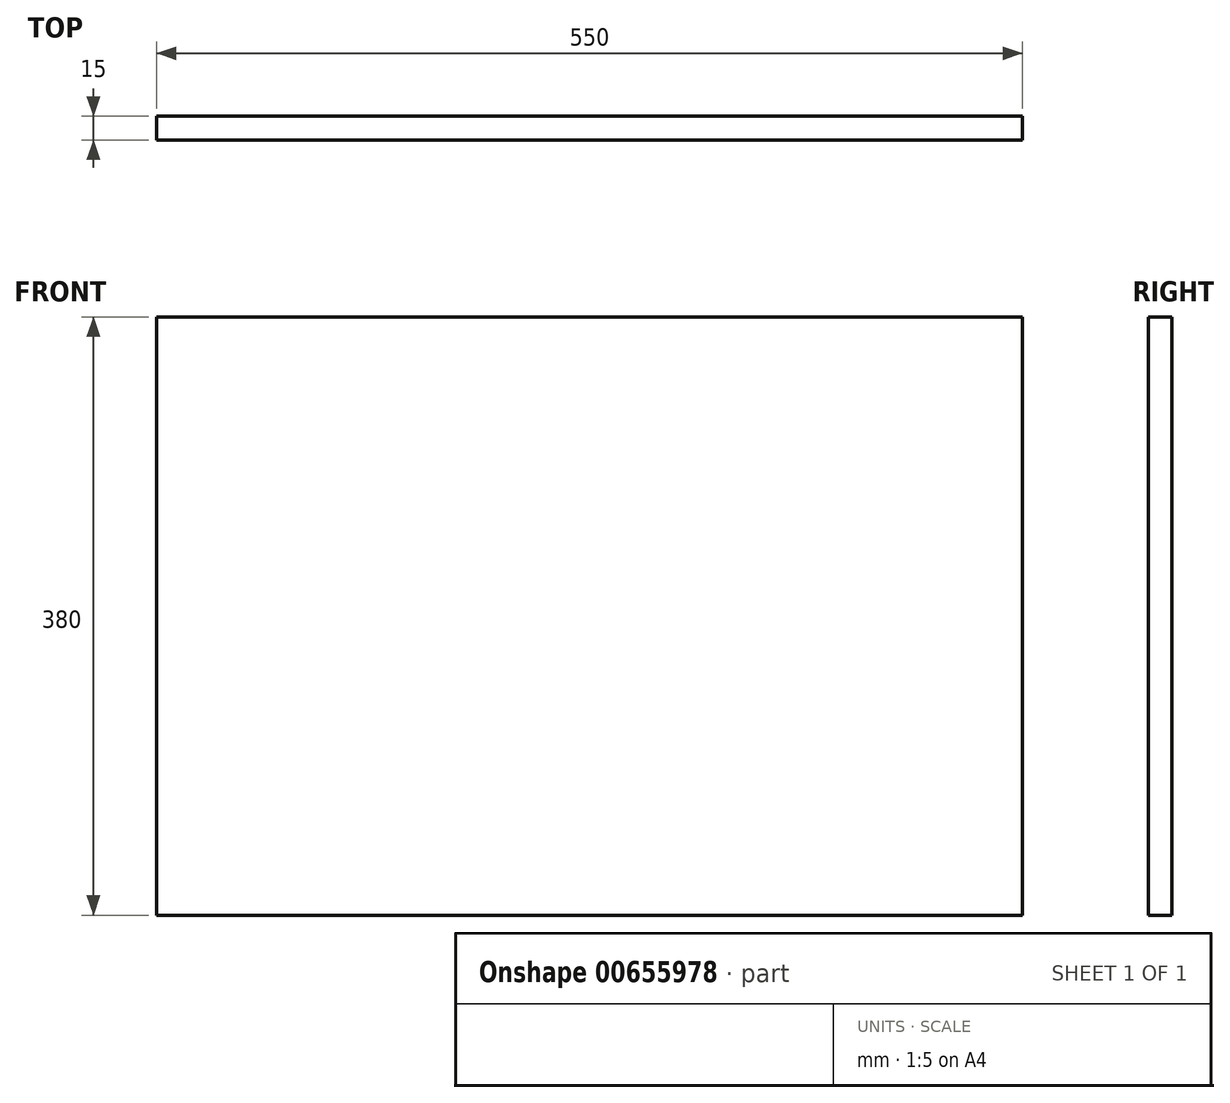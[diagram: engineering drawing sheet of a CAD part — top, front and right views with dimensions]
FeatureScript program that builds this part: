
annotation { "Feature Type Name" : "Feature", "Feature Type Description" : "" }
export const myFeature = defineFeature(function(context is Context, id is Id, definition is map)
    precondition{}
    {
        {
            var Q0;
            Q0=qCreatedBy(makeId("Front.planeOp"),FACE);
            var sketch = newSketch(context, id + "F0", { "sketchPlane" : qUnion([Q0])});
            skLineSegment(sketch, "E0.bottom", {"start": v(0, 0) * mm, "end": v(550, 0) * mm});
            skLineSegment(sketch, "E0.top", {"start": v(0, 380) * mm, "end": v(550, 380) * mm});
            skLineSegment(sketch, "E0.left", {"start": v(0, 0) * mm, "end": v(0, 380) * mm});
            skLineSegment(sketch, "E0.right", {"start": v(550, 0) * mm, "end": v(550, 380) * mm});
            skSolve(sketch);
        }
        {
            var Q0;
            Q0=makeQuery(id+"F0.imprint","IMPRINT",FACE,{"disambiguationData":[TD([[makeQuery(id+"F0.imprint","IMPRINT",EDGE,{"derivedFrom":sQuery(id+"F0.wireOp",EDGE,"E0.bottom")}),1.0]])]});
            extrude(context, id + "F1", {"entities" : qUnion([Q0]), "depth" : 15 * mm, "offsetDistance" : 25.4 * mm});
        }
    });
